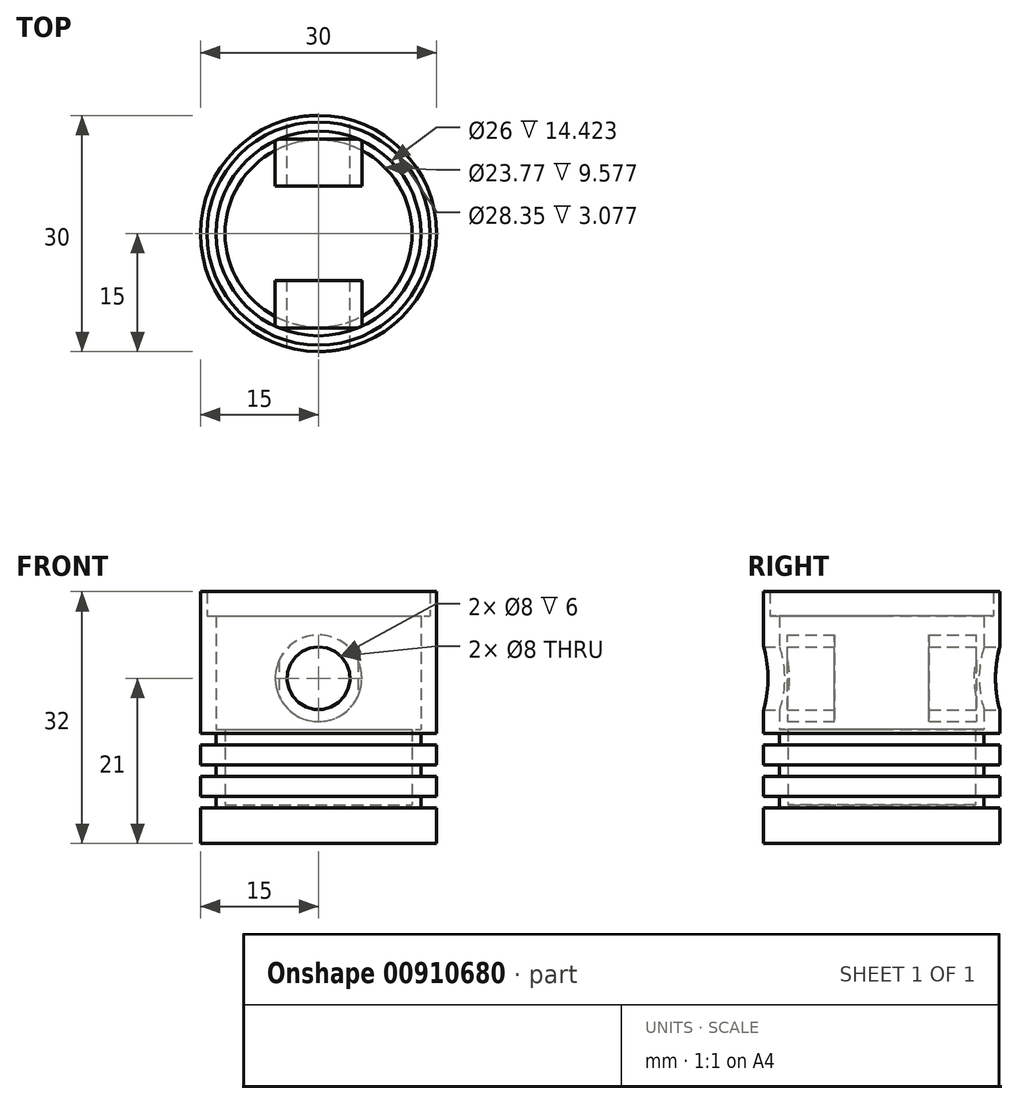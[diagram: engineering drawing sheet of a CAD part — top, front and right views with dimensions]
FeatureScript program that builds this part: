
annotation { "Feature Type Name" : "Feature", "Feature Type Description" : "" }
export const myFeature = defineFeature(function(context is Context, id is Id, definition is map)
    precondition{}
    {
        {
            var Q0;
            Q0=qCreatedBy(makeId("Front.planeOp"),FACE);
            var sketch = newSketch(context, id + "F0", { "sketchPlane" : qUnion([Q0])});
            skLineSegment(sketch, "E0", {"start": v(0, 0) * mm, "end": v(-15, 0) * mm});
            skLineSegment(sketch, "E1", {"start": v(-15, 0) * mm, "end": v(-15, 4.5) * mm});
            skLineSegment(sketch, "E2", {"start": v(-15, 4.5) * mm, "end": v(-13, 4.5) * mm});
            skLineSegment(sketch, "E3", {"start": v(-13, 4.5) * mm, "end": v(-13, 6) * mm});
            skLineSegment(sketch, "E4", {"start": v(-13, 6) * mm, "end": v(-15, 6) * mm});
            skLineSegment(sketch, "E5", {"start": v(-15, 6) * mm, "end": v(-15, 8.5) * mm});
            skLineSegment(sketch, "E6", {"start": v(-15, 8.5) * mm, "end": v(-13, 8.5) * mm});
            skLineSegment(sketch, "E7", {"start": v(-13, 8.5) * mm, "end": v(-13, 10) * mm});
            skLineSegment(sketch, "E8", {"start": v(-13, 10) * mm, "end": v(-15, 10) * mm});
            skLineSegment(sketch, "E9", {"start": v(-15, 10) * mm, "end": v(-15, 12.5) * mm});
            skLineSegment(sketch, "E10", {"start": v(-15, 12.5) * mm, "end": v(-13, 12.5) * mm});
            skLineSegment(sketch, "E11", {"start": v(-13, 12.5) * mm, "end": v(-13, 14) * mm});
            skLineSegment(sketch, "E12", {"start": v(-13, 14) * mm, "end": v(-15, 14) * mm});
            skLineSegment(sketch, "E13", {"start": v(-15, 14) * mm, "end": v(-15, 32) * mm});
            skLineSegment(sketch, "E14", {"start": v(-11.89, 4.92) * mm, "end": v(0, 4.92) * mm});
            skLineSegment(sketch, "E15", {"start": v(0, 0) * mm, "end": v(0, 4.92) * mm});
            skLineSegment(sketch, "E16", {"start": v(-13, 14.5) * mm, "end": v(-11.89, 14.5) * mm});
            skLineSegment(sketch, "E17", {"start": v(-11.89, 4.92) * mm, "end": v(-11.89, 14.5) * mm});
            skLineSegment(sketch, "E18", {"start": v(-13, 14.5) * mm, "end": v(-13, 28.92) * mm});
            skLineSegment(sketch, "E19", {"start": v(-13, 28.92) * mm, "end": v(-14.18, 28.92) * mm});
            skLineSegment(sketch, "E20", {"start": v(-14.18, 28.92) * mm, "end": v(-14.18, 32) * mm});
            skLineSegment(sketch, "E21", {"start": v(-14.18, 32) * mm, "end": v(-15, 32) * mm});
            skSolve(sketch);
        }
        {
            var Q0;
            Q0=makeQuery(id+"F0.imprint","IMPRINT",FACE,{"disambiguationData":[TD([[makeQuery(id+"F0.imprint","IMPRINT",EDGE,{"derivedFrom":sQuery(id+"F0.wireOp",EDGE,"E0")}),-1.0]])]});
            var Q1;
            Q1=sQuery(id+"F0.wireOp",EDGE,"E15");
            revolve(context, id + "F1", {"surfaceOperationType" : NewSurfaceOperationType.NEW, "entities" : qUnion([Q0]), "axis" : qUnion([Q1]), "revolveType" : RevolveType.FULL});
        }
        {
            var Q0;
            Q0=qCreatedBy(makeId("Front.planeOp"),FACE);
            var sketch = newSketch(context, id + "F2", { "sketchPlane" : qUnion([Q0])});
            skLineSegment(sketch, "E22", {"start": v(0, 0) * mm, "end": v(0, 12) * mm});
            skLineSegment(sketch, "E23", {"start": v(0, 12) * mm, "end": v(0, 21) * mm});
            skCircle(sketch, "E24", {"center": v(0, 21) * mm, "radius": 4 * mm});
            skCircle(sketch, "E25", {"center": v(0, 21) * mm, "radius": 5.5 * mm});
            skSolve(sketch);
        }
        {
            var Q0;
            Q0=makeQuery(id+"F2.imprint","IMPRINT",FACE,{"disambiguationData":[TD([[makeQuery(id+"F2.imprint","IMPRINT",EDGE,{"derivedFrom":sQuery(id+"F2.wireOp",EDGE,"E24")}),1.0]])]});
            extrude(context, id + "F3", {"entities" : qUnion([Q0]), "operationType" : NewBodyOperationType.REMOVE, "endBound" : BoundingType.SYMMETRIC, "depth" : 40 * mm, "offsetDistance" : 25 * mm});
        }
        {
            var Q0;
            Q0=makeQuery(id+"F2.imprint","IMPRINT",FACE,{"disambiguationData":[TD([[makeQuery(id+"F2.imprint","IMPRINT",EDGE,{"derivedFrom":sQuery(id+"F2.wireOp",EDGE,"E24")}),-1.0]])]});
            extrude(context, id + "F4", {"entities" : qUnion([Q0]), "operationType" : NewBodyOperationType.ADD, "endBound" : BoundingType.SYMMETRIC, "depth" : 24 * mm, "offsetDistance" : 25 * mm});
        }
        {
            var Q0;
            Q0=qSketchRegion(id+"F2",true);
            extrude(context, id + "F5", {"entities" : qUnion([Q0]), "operationType" : NewBodyOperationType.REMOVE, "endBound" : BoundingType.SYMMETRIC, "oppositeDirection" : true, "depth" : 12 * mm, "offsetDistance" : 25 * mm});
        }
    });
